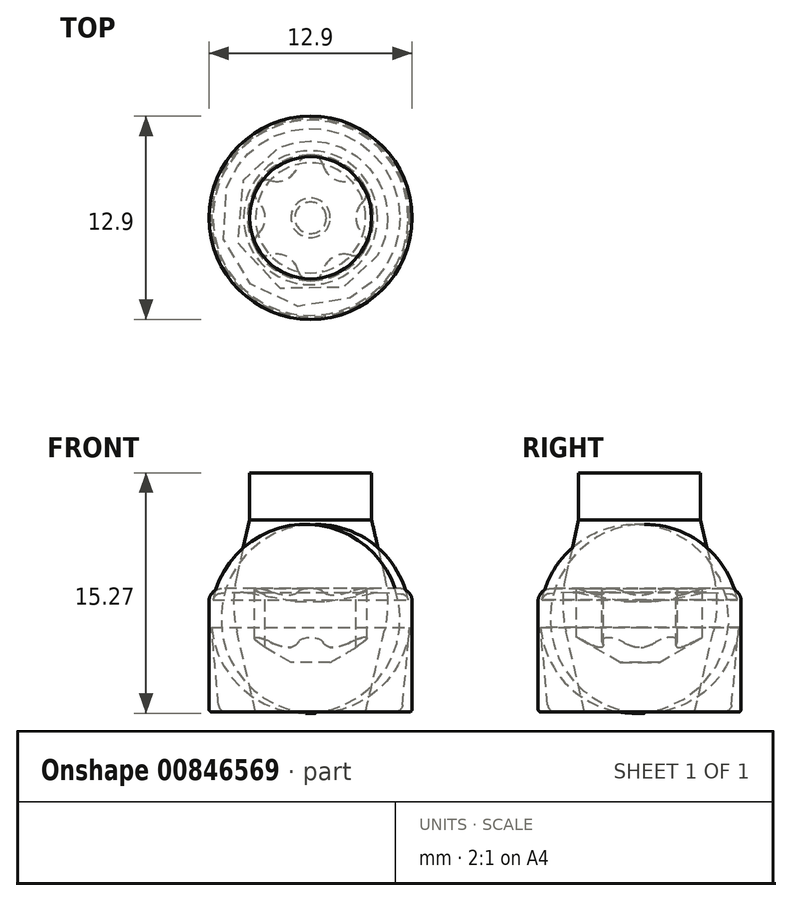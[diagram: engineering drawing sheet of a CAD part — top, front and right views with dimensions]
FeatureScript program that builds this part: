
annotation { "Feature Type Name" : "Feature", "Feature Type Description" : "" }
export const myFeature = defineFeature(function(context is Context, id is Id, definition is map)
    precondition{}
    {
        {
            var Q0;
            Q0=qCreatedBy(makeId("Front.planeOp"),FACE);
            var sketch = newSketch(context, id + "F0", { "sketchPlane" : qUnion([Q0])});
            skLineSegment(sketch, "E0", {"start": v(0, 0) * mm, "end": v(0, 3.16) * mm, "construction": true});
            skLineSegment(sketch, "E1", {"start": v(4, 7.85) * mm, "end": v(5.65, 7.85) * mm});
            skLineSegment(sketch, "E2", {"start": v(6.45, 7.05) * mm, "end": v(6.45, 0.2) * mm});
            skLineSegment(sketch, "E3", {"start": v(6.25, 0) * mm, "end": v(0, 0) * mm});
            skPoint(sketch, "E4.visualSharp", {"position": v(6.45, 7.85) * mm});
            skArc(sketch, "E4.filletArc", {"start": v(6.45, 7.05) * mm, "mid": v(6.22, 7.62) * mm, "end": v(5.65, 7.85) * mm});
            skPoint(sketch, "E5.visualSharp", {"position": v(6.45, 0) * mm});
            skArc(sketch, "E5.filletArc", {"start": v(6.25, 0) * mm, "mid": v(6.4, 0.06) * mm, "end": v(6.45, 0.2) * mm});
            skLineSegment(sketch, "E6", {"start": v(4, 7.85) * mm, "end": v(4, 4.75) * mm});
            skLineSegment(sketch, "E7", {"start": v(4, 4.75) * mm, "end": v(1.25, 3.16) * mm});
            skLineSegment(sketch, "E8", {"start": v(1.25, 3.16) * mm, "end": v(0, 3.16) * mm});
            skLineSegment(sketch, "E9", {"start": v(0, 3.16) * mm, "end": v(0, 0) * mm});
            skSolve(sketch);
        }
        {
            var Q0;
            Q0=qSketchRegion(id+"F0",true);
            var Q1;
            Q1=sQuery(id+"F0.wireOp",EDGE,"E9");
            revolve(context, id + "F1", {"surfaceOperationType" : NewSurfaceOperationType.NEW, "entities" : qUnion([Q0]), "axis" : qUnion([Q1]), "revolveType" : RevolveType.FULL});
        }
        {
            var Q0;
            Q0=makeQuery(id+"F1.opRevolve","SWEPT_FACE",FACE,{"disambiguationData":[OSD([sQuery(id+"F0.wireOp",EDGE,"E1")])]});
            var sketch = newSketch(context, id + "F2", { "sketchPlane" : qUnion([Q0])});
            skArc(sketch, "E10", {"start": v(0.77, 3.4) * mm, "mid": v(0, 4) * mm, "end": v(-0.77, 3.4) * mm});
            skLineSegment(sketch, "E11", {"start": v(-0.77, 3.4) * mm, "end": v(-0.79, 3.35) * mm});
            skLineSegment(sketch, "E12", {"start": v(0.77, 3.4) * mm, "end": v(0.79, 3.35) * mm});
            skLineSegment(sketch, "E13.1.0", {"start": v(-2.56, 2.37) * mm, "end": v(-2.5, 2.36) * mm});
            skArc(sketch, "E13.1.1", {"start": v(-2.56, 2.37) * mm, "mid": v(-3.46, 2) * mm, "end": v(-3.34, 1.03) * mm});
            skLineSegment(sketch, "E13.1.2", {"start": v(-3.34, 1.03) * mm, "end": v(-3.3, 0.99) * mm});
            skLineSegment(sketch, "E13.2.0", {"start": v(-3.34, -1.03) * mm, "end": v(-3.3, -0.99) * mm});
            skArc(sketch, "E13.2.1", {"start": v(-3.34, -1.03) * mm, "mid": v(-3.46, -2) * mm, "end": v(-2.56, -2.37) * mm});
            skLineSegment(sketch, "E13.2.2", {"start": v(-2.56, -2.37) * mm, "end": v(-2.5, -2.36) * mm});
            skLineSegment(sketch, "E13.3.0", {"start": v(-0.77, -3.4) * mm, "end": v(-0.79, -3.35) * mm});
            skArc(sketch, "E13.3.1", {"start": v(-0.77, -3.4) * mm, "mid": v(0, -4) * mm, "end": v(0.77, -3.4) * mm});
            skLineSegment(sketch, "E13.3.2", {"start": v(0.77, -3.4) * mm, "end": v(0.79, -3.35) * mm});
            skLineSegment(sketch, "E13.4.0", {"start": v(2.56, -2.37) * mm, "end": v(2.5, -2.36) * mm});
            skArc(sketch, "E13.4.1", {"start": v(2.56, -2.37) * mm, "mid": v(3.46, -2) * mm, "end": v(3.34, -1.03) * mm});
            skLineSegment(sketch, "E13.4.2", {"start": v(3.34, -1.03) * mm, "end": v(3.3, -0.99) * mm});
            skLineSegment(sketch, "E13.5.0", {"start": v(3.34, 1.03) * mm, "end": v(3.3, 0.99) * mm});
            skArc(sketch, "E13.5.1", {"start": v(3.34, 1.03) * mm, "mid": v(3.46, 2) * mm, "end": v(2.56, 2.37) * mm});
            skLineSegment(sketch, "E13.5.2", {"start": v(2.56, 2.37) * mm, "end": v(2.5, 2.36) * mm});
            skPoint(sketch, "E13.center", {"position": v(0, 0) * mm});
            skPoint(sketch, "E14.newPointA", {"position": v(-0.26, 1.75) * mm});
            skPoint(sketch, "E14.newPointB", {"position": v(-1.4, 1.1) * mm});
            skArc(sketch, "E14.filletArc", {"start": v(-2.5, 2.36) * mm, "mid": v(-1.44, 2.5) * mm, "end": v(-0.79, 3.35) * mm});
            skPoint(sketch, "E15.newPointA", {"position": v(0.25, 1.75) * mm});
            skPoint(sketch, "E15.newPointB", {"position": v(1.4, 1.1) * mm});
            skArc(sketch, "E15.filletArc", {"start": v(0.79, 3.35) * mm, "mid": v(1.44, 2.5) * mm, "end": v(2.5, 2.36) * mm});
            skPoint(sketch, "E16.newPointA", {"position": v(1.65, -0.65) * mm});
            skPoint(sketch, "E16.newPointB", {"position": v(1.64, 0.66) * mm});
            skArc(sketch, "E16.filletArc", {"start": v(3.3, 0.99) * mm, "mid": v(2.88, 0) * mm, "end": v(3.3, -0.99) * mm});
            skPoint(sketch, "E17.newPointA", {"position": v(0.26, -1.75) * mm});
            skPoint(sketch, "E17.newPointB", {"position": v(1.4, -1.1) * mm});
            skArc(sketch, "E17.filletArc", {"start": v(2.5, -2.36) * mm, "mid": v(1.44, -2.5) * mm, "end": v(0.79, -3.35) * mm});
            skPoint(sketch, "E18.newPointA", {"position": v(-1.4, -1.1) * mm});
            skPoint(sketch, "E18.newPointB", {"position": v(-0.25, -1.75) * mm});
            skArc(sketch, "E18.filletArc", {"start": v(-0.79, -3.35) * mm, "mid": v(-1.44, -2.5) * mm, "end": v(-2.5, -2.36) * mm});
            skPoint(sketch, "E19.newPointA", {"position": v(-1.65, 0.65) * mm});
            skPoint(sketch, "E19.newPointB", {"position": v(-1.64, -0.66) * mm});
            skArc(sketch, "E19.filletArc", {"start": v(-3.3, -0.99) * mm, "mid": v(-2.88, 0) * mm, "end": v(-3.3, 0.99) * mm});
            skCircle(sketch, "E20", {"center": v(0, 0) * mm, "radius": 4.28 * mm});
            skSolve(sketch);
        }
        {
            var Q0;
            Q0=qSketchRegion(id+"F2",true);
            var Q1;
            Q1=makeQuery(id+"F1.opRevolve","SWEPT_FACE",FACE,{"disambiguationData":[OSD([sQuery(id+"F0.wireOp",EDGE,"E7")])]});
            extrude(context, id + "F3", {"entities" : qUnion([Q0]), "operationType" : NewBodyOperationType.ADD, "endBound" : BoundingType.UP_TO_SURFACE, "oppositeDirection" : true, "endBoundEntityFace" : qUnion([Q1]), "offsetDistance" : 25 * mm, "depth" : 25 * mm});
        }
        {
            var Q0;
            Q0=makeQuery(id+"F3.boolean.opBoolean","MERGE",FACE,{"derivedFrom":[makeQuery(id+"F1.opRevolve","SWEPT_FACE",FACE,{"disambiguationData":[OSD([sQuery(id+"F0.wireOp",EDGE,"E1")])]}),makeQuery(id+"F3.opExtrude","CAP_FACE",FACE,{"disambiguationData":[OSD([sQuery(id+"F2.wireOp",EDGE,"E10"),sQuery(id+"F2.wireOp",EDGE,"E11"),sQuery(id+"F2.wireOp",EDGE,"E12"),sQuery(id+"F2.wireOp",EDGE,"E13.1.0"),sQuery(id+"F2.wireOp",EDGE,"E13.1.1"),sQuery(id+"F2.wireOp",EDGE,"E13.1.2"),sQuery(id+"F2.wireOp",EDGE,"E13.2.0"),sQuery(id+"F2.wireOp",EDGE,"E13.2.1"),sQuery(id+"F2.wireOp",EDGE,"E13.2.2"),sQuery(id+"F2.wireOp",EDGE,"E13.3.0"),sQuery(id+"F2.wireOp",EDGE,"E13.3.1"),sQuery(id+"F2.wireOp",EDGE,"E13.3.2"),sQuery(id+"F2.wireOp",EDGE,"E13.4.0"),sQuery(id+"F2.wireOp",EDGE,"E13.4.1"),sQuery(id+"F2.wireOp",EDGE,"E13.4.2"),sQuery(id+"F2.wireOp",EDGE,"E13.5.0"),sQuery(id+"F2.wireOp",EDGE,"E13.5.1"),sQuery(id+"F2.wireOp",EDGE,"E13.5.2"),sQuery(id+"F2.wireOp",EDGE,"E14.filletArc"),sQuery(id+"F2.wireOp",EDGE,"E15.filletArc"),sQuery(id+"F2.wireOp",EDGE,"E16.filletArc"),sQuery(id+"F2.wireOp",EDGE,"E17.filletArc"),sQuery(id+"F2.wireOp",EDGE,"E18.filletArc"),sQuery(id+"F2.wireOp",EDGE,"E19.filletArc"),sQuery(id+"F2.wireOp",EDGE,"E20")])],"isStart":true})]});
            var sketch = newSketch(context, id + "F4", { "sketchPlane" : qUnion([Q0])});
            skCircle(sketch, "E21", {"center": v(0, 0) * mm, "radius": 4 * mm});
            skSolve(sketch);
        }
        {
            var Q0;
            Q0=qSketchRegion(id+"F4",true);
            extrude(context, id + "F5", {"entities" : qUnion([Q0]), "operationType" : NewBodyOperationType.REMOVE, "oppositeDirection" : true, "offsetDistance" : 25 * mm, "depth" : 1 * mm, "hasDraft" : true, "draftAngle" : 70 * degree, "draftPullDirection" : true});
        }
        {
            var Q0;
            Q0=qCreatedBy(makeId("Front.planeOp"),FACE);
            var sketch = newSketch(context, id + "F6", { "sketchPlane" : qUnion([Q0])});
            skLineSegment(sketch, "E22", {"start": v(0, 0) * mm, "end": v(0, 15.2) * mm, "construction": true});
            skLineSegment(sketch, "E23", {"start": v(0, 15.2) * mm, "end": v(3.87, 15.2) * mm});
            skLineSegment(sketch, "E24", {"start": v(3.87, 15.2) * mm, "end": v(3.87, 12.2) * mm});
            skLineSegment(sketch, "E25", {"start": v(3.87, 12.2) * mm, "end": v(4.68, 8.72) * mm});
            skLineSegment(sketch, "E26", {"start": v(3.5, 0) * mm, "end": v(0, 0) * mm});
            skLineSegment(sketch, "E27", {"start": v(0, 15.2) * mm, "end": v(0, 0) * mm});
            skLineSegment(sketch, "E28", {"start": v(3.5, 0) * mm, "end": v(4.68, 5.12) * mm});
            skArc(sketch, "E29.filletArc", {"start": v(4.68, 5.12) * mm, "mid": v(4.88, 6.92) * mm, "end": v(4.68, 8.72) * mm});
            skSolve(sketch);
        }
        {
            var Q0;
            Q0=qSketchRegion(id+"F6",true);
            var Q1;
            Q1=sQuery(id+"F6.wireOp",EDGE,"E27");
            revolve(context, id + "F7", {"entities" : qUnion([Q0]), "axis" : qUnion([Q1]), "revolveType" : RevolveType.FULL});
        }
        {
            var Q0;
            Q0=qCreatedBy(makeId("Front.planeOp"),FACE);
            var sketch = newSketch(context, id + "F8", { "sketchPlane" : qUnion([Q0])});
            skLineSegment(sketch, "E30", {"start": v(0, 0) * mm, "end": v(0, 7.03) * mm});
            skLineSegment(sketch, "E31", {"start": v(6.3, 5.39) * mm, "end": v(5.84, 0.45) * mm});
            skLineSegment(sketch, "E32", {"start": v(5.34, 0) * mm, "end": v(0, 0) * mm});
            skPoint(sketch, "E33.visualSharp", {"position": v(5.8, 0) * mm});
            skArc(sketch, "E33.filletArc", {"start": v(5.34, 0) * mm, "mid": v(5.68, 0.13) * mm, "end": v(5.84, 0.45) * mm});
            skLineSegment(sketch, "E34", {"start": v(0, 7.03) * mm, "end": v(0, 0) * mm, "construction": true});
            skLineSegment(sketch, "E35", {"start": v(0, 7.03) * mm, "end": v(1, 7.03) * mm});
            skLineSegment(sketch, "E36", {"start": v(1, 7.03) * mm, "end": v(4.25, 7.6) * mm});
            skLineSegment(sketch, "E37", {"start": v(4.25, 7.6) * mm, "end": v(5.74, 7.52) * mm});
            skArc(sketch, "E38.filletArc", {"start": v(6.3, 5.39) * mm, "mid": v(6.31, 6.26) * mm, "end": v(6.2, 7.12) * mm});
            skPoint(sketch, "E39.visualSharp", {"position": v(6.11, 7.5) * mm});
            skArc(sketch, "E39.filletArc", {"start": v(6.2, 7.12) * mm, "mid": v(6.04, 7.4) * mm, "end": v(5.74, 7.52) * mm});
            skLineSegment(sketch, "E40", {"start": v(6.3, 5.39) * mm, "end": v(6.35, 6) * mm, "construction": true});
            skSolve(sketch);
        }
        {
            var Q0;
            Q0=qSketchRegion(id+"F8",true);
            var Q1;
            Q1=sQuery(id+"F8.wireOp",EDGE,"E30");
            revolve(context, id + "F9", {"entities" : qUnion([Q0]), "axis" : qUnion([Q1]), "revolveType" : RevolveType.FULL});
        }
    });
